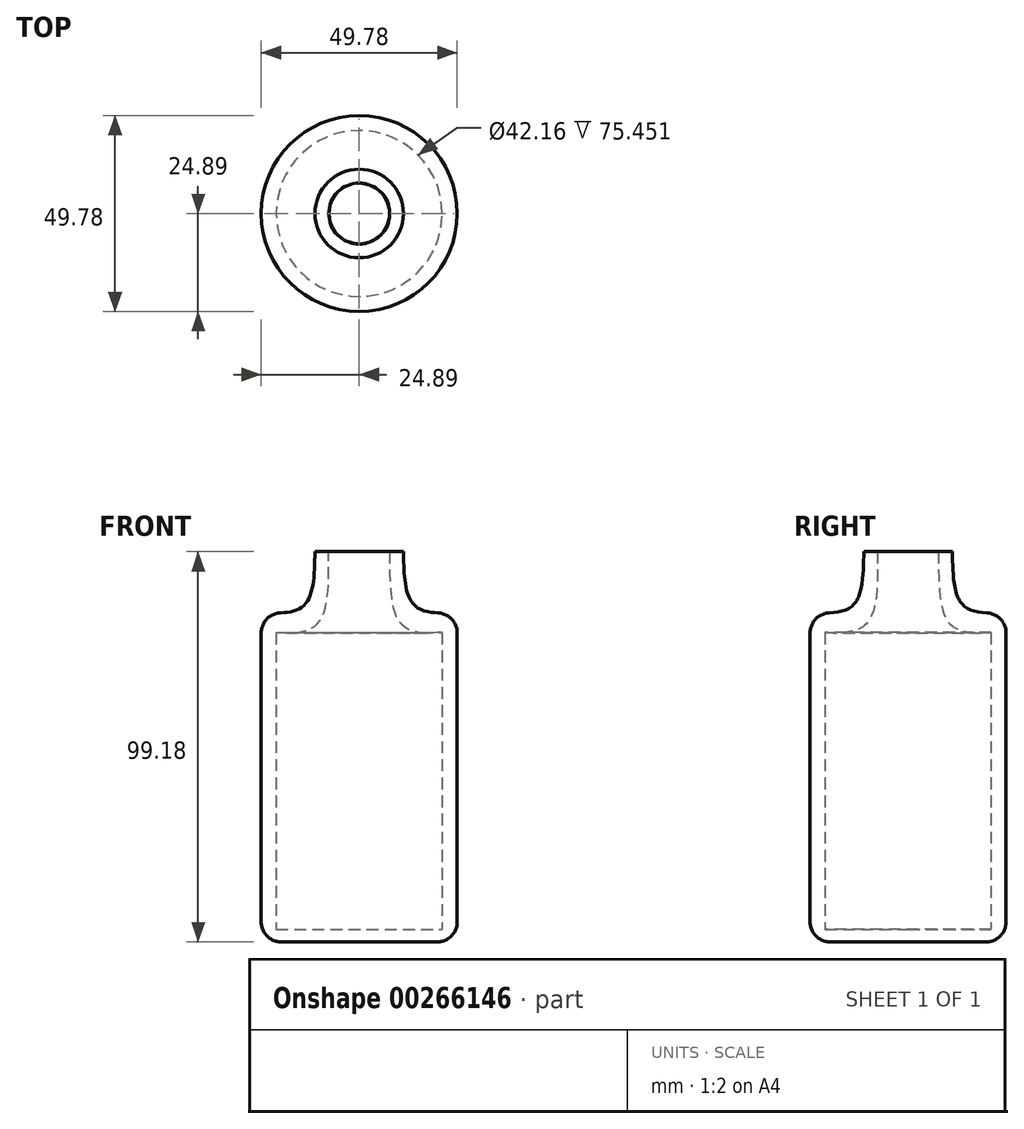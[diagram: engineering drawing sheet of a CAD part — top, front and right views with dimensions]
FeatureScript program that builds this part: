
annotation { "Feature Type Name" : "Feature", "Feature Type Description" : "" }
export const myFeature = defineFeature(function(context is Context, id is Id, definition is map)
    precondition{}
    {
        {
            var Q0;
            Q0=qCreatedBy(makeId("Front.planeOp"),FACE);
            var sketch = newSketch(context, id + "F0", { "sketchPlane" : qUnion([Q0])});
            skLineSegment(sketch, "E0", {"start": v(-24.89, 31.9) * mm, "end": v(-24.89, -51.8) * mm});
            skLineSegment(sketch, "E1", {"start": v(-24.89, -51.8) * mm, "end": v(0, -51.8) * mm});
            skLineSegment(sketch, "E2", {"start": v(0, -51.8) * mm, "end": v(0, 47.38) * mm});
            skLineSegment(sketch, "E3", {"start": v(0, 47.38) * mm, "end": v(-11.25, 47.38) * mm});
            skFitSpline(sketch, "E4", {"points": [v(-24.89, 31.9) * mm, v(-14.01, 33.74) * mm, v(-11.25, 47.38) * mm], "startDerivative": vector(27.3, -1.24) * mm, "endDerivative": vector(0.5, 31.57) * mm});
            skLineSegment(sketch, "E5", {"start": v(-21.08, -48.65) * mm, "end": v(0, -48.65) * mm});
            skLineSegment(sketch, "E6", {"start": v(0, -48.65) * mm, "end": v(-21.08, -48.65) * mm});
            skLineSegment(sketch, "E7", {"start": v(-21.08, -48.65) * mm, "end": v(-21.08, 26.8) * mm});
            skFitSpline(sketch, "E8", {"points": [v(-21.08, 26.8) * mm, v(-10.65, 28.98) * mm, v(-7.75, 47.38) * mm], "startDerivative": vector(28.33, -0.8) * mm, "endDerivative": vector(-0.34, 40.06) * mm});
            skSolve(sketch);
        }
        {
            var Q0;
            Q0=makeQuery(id+"F0.imprint","IMPRINT",FACE,{"disambiguationData":[TD([[makeQuery(id+"F0.imprint","IMPRINT",EDGE,{"derivedFrom":sQuery(id+"F0.wireOp",EDGE,"E0")}),1.0]])]});
            var Q1;
            Q1=sQuery(id+"F0.wireOp",EDGE,"E2");
            revolve(context, id + "F1", {"entities" : qUnion([Q0]), "axis" : qUnion([Q1]), "revolveType" : RevolveType.FULL});
        }
        {
            var Q0;
            Q0=makeQuery(id+"F1.opRevolve","SWEPT_EDGE",EDGE,{"disambiguationData":[OSD([sQuery(id+"F0.wireOp",EDGE,"E0"),sQuery(id+"F0.wireOp",EDGE,"E4")])]});
            var Q1;
            Q1=makeQuery(id+"F1.opRevolve","SWEPT_EDGE",EDGE,{"disambiguationData":[OSD([sQuery(id+"F0.wireOp",EDGE,"E0"),sQuery(id+"F0.wireOp",EDGE,"E1")])]});
            fillet(context, id + "F2", {"entities" : qUnion([Q0, Q1]), "radius" : 5.08 * mm, "tangentPropagation" : true, "allowEdgeOverflow" : false});
        }
    });
